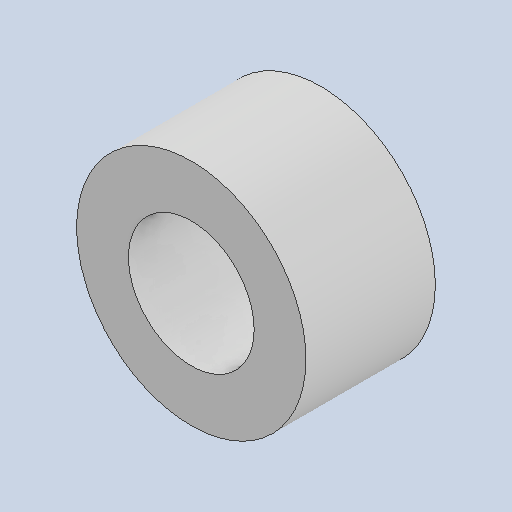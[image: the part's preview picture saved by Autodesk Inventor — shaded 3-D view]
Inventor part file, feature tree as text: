
AUTODESK INVENTOR PART (.ipt)
format: ipt  version: 2024 (Build 280153000, 153)  size: 96,256 bytes
history: native  units: in
note: dims shown in document units (in); Inventor stores cm internally (conversion verified against a paired STEP export)
features: other x3, sketch x1
ambient origin geometry x8: Origin, YZ Plane, XZ Plane, XY Plane, X Axis, Y Axis, Z Axis, Center Point
bodies: Solid1 (feature_tree)
feature tree (4):
  other  "Part2.ipt"
  other  "Solid1::Part2.ipt"
  other  "TaggingFeature1"
  sketch  "Sketch1"  dims[d0=0.3937in]
